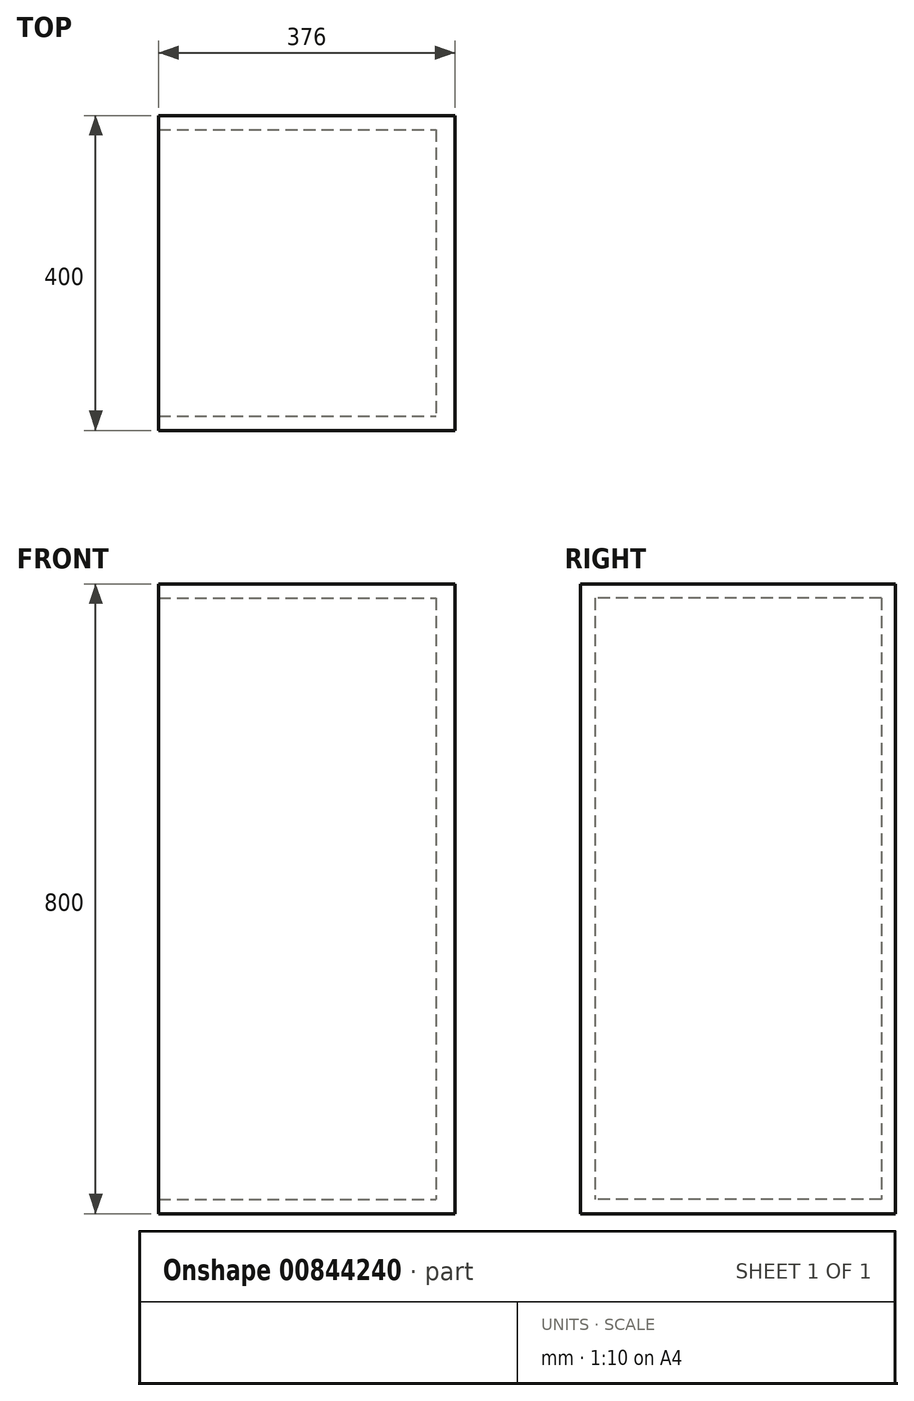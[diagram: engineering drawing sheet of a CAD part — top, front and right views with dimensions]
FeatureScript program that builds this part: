
annotation { "Feature Type Name" : "Feature", "Feature Type Description" : "" }
export const myFeature = defineFeature(function(context is Context, id is Id, definition is map)
    precondition{}
    {
        {
            var Q0;
            Q0=qCreatedBy(makeId("Top.planeOp"),FACE);
            var sketch = newSketch(context, id + "F0", { "sketchPlane" : qUnion([Q0])});
            skLineSegment(sketch, "E0.bottom", {"start": v(0, 0) * mm, "end": v(42.8, 0) * mm});
            skLineSegment(sketch, "E0.top", {"start": v(0, -46.9) * mm, "end": v(42.8, -46.9) * mm});
            skLineSegment(sketch, "E0.left", {"start": v(0, 0) * mm, "end": v(0, -46.9) * mm});
            skLineSegment(sketch, "E0.right", {"start": v(42.8, 0) * mm, "end": v(42.8, -46.9) * mm});
            skSolve(sketch);
        }
        {
            var Q0;
            Q0=makeQuery(id+"F0.imprint","IMPRINT",FACE,{"disambiguationData":[TD([[makeQuery(id+"F0.imprint","IMPRINT",EDGE,{"derivedFrom":sQuery(id+"F0.wireOp",EDGE,"E0.bottom")}),-1.0]])]});
            extrude(context, id + "F1", {"entities" : qUnion([Q0]), "depth" : 800 * mm, "offsetDistance" : 25 * mm});
        }
        {
            var Q0;
            Q0=makeQuery(id+"F1.opExtrude","SWEPT_FACE",FACE,{"disambiguationData":[OSD([sQuery(id+"F0.wireOp",EDGE,"E0.bottom")])]});
            extrude(context, id + "F2", {"entities" : qUnion([Q0]), "operationType" : NewBodyOperationType.ADD, "oppositeDirection" : true, "depth" : 400 * mm, "offsetDistance" : 25 * mm});
        }
        {
            var Q0;
            {var subQ0=sQuery(id+"F0.wireOp",EDGE,"E0.left");Q0=makeQuery(id+"F2.boolean.opBoolean","MERGE",FACE,{"derivedFrom":[makeQuery(id+"F1.opExtrude","SWEPT_FACE",FACE,{"disambiguationData":[OSD([subQ0])]}),makeQuery(id+"F2.opExtrude","SWEPT_FACE",FACE,{"disambiguationData":[OSD([sQuery(id+"F0.wireOp",EDGE,"E0.bottom"),subQ0])]})]});}
            extrude(context, id + "F3", {"entities" : qUnion([Q0]), "operationType" : NewBodyOperationType.ADD, "depth" : 100 * mm, "offsetDistance" : 25 * mm});
        }
        {
            var Q0;
            {var subQ0=sQuery(id+"F0.wireOp",EDGE,"E0.right");Q0=makeQuery(id+"F2.boolean.opBoolean","MERGE",FACE,{"derivedFrom":[makeQuery(id+"F1.opExtrude","SWEPT_FACE",FACE,{"disambiguationData":[OSD([subQ0])]}),makeQuery(id+"F2.opExtrude","SWEPT_FACE",FACE,{"disambiguationData":[OSD([sQuery(id+"F0.wireOp",EDGE,"E0.bottom"),subQ0])]})]});}
            extrude(context, id + "F4", {"entities" : qUnion([Q0]), "operationType" : NewBodyOperationType.REMOVE, "oppositeDirection" : true, "depth" : 42.8 * mm, "offsetDistance" : 25 * mm});
        }
        {
            var Q0;
            Q0=makeQuery(id+"F4.boolean.opBoolean","COPY",FACE,{"derivedFrom":makeQuery(id+"F4.opExtrude","CAP_FACE",FACE,{"disambiguationData":[OSD([sQuery(id+"F0.wireOp",EDGE,"E0.bottom"),sQuery(id+"F0.wireOp",EDGE,"E0.right")])],"isStart":false})});
            extrude(context, id + "F5", {"entities" : qUnion([Q0]), "operationType" : NewBodyOperationType.ADD, "oppositeDirection" : true, "depth" : 370 * mm, "offsetDistance" : 25 * mm});
        }
        {
            var Q0;
            Q0=makeQuery(id+"F5.opExtrude","CAP_FACE",FACE,{"disambiguationData":[OSD([sQuery(id+"F0.wireOp",EDGE,"E0.bottom"),sQuery(id+"F0.wireOp",EDGE,"E0.right")])],"isStart":false});
            shell(context, id + "F6", {"entities" : qUnion([Q0]), "thickness" : 18 * mm});
        }
        {
            var Q0;
            Q0=makeQuery(id+"F4.boolean.opBoolean","COPY",FACE,{"derivedFrom":makeQuery(id+"F4.opExtrude","CAP_FACE",FACE,{"disambiguationData":[OSD([sQuery(id+"F0.wireOp",EDGE,"E0.bottom"),sQuery(id+"F0.wireOp",EDGE,"E0.right")])],"isStart":false})});
            extrude(context, id + "F7", {"entities" : qUnion([Q0]), "operationType" : NewBodyOperationType.ADD, "depth" : 6 * mm, "offsetDistance" : 25 * mm});
        }
    });
